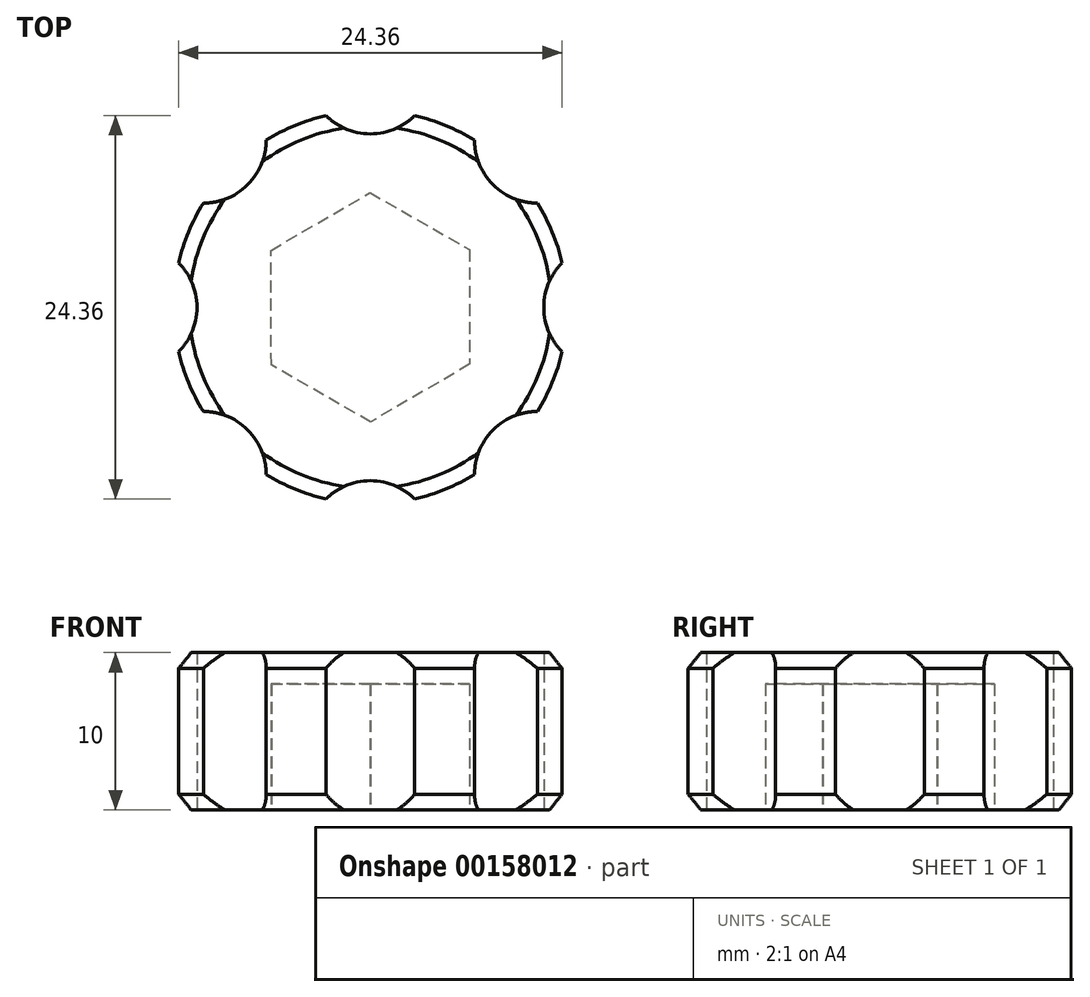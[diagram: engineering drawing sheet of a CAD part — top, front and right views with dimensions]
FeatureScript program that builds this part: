
annotation { "Feature Type Name" : "Feature", "Feature Type Description" : "" }
export const myFeature = defineFeature(function(context is Context, id is Id, definition is map)
    precondition{}
    {
        {
            var Q0;
            Q0=qCreatedBy(makeId("Top.planeOp"),FACE);
            var sketch = newSketch(context, id + "F0", { "sketchPlane" : qUnion([Q0])});
            skCircle(sketch, "E0", {"center": v(0, 0) * mm, "radius": 12.5 * mm});
            skCircle(sketch, "E1.cCircle", {"center": v(0, 0) * mm, "radius": 6.3 * mm, "construction": true});
            skLineSegment(sketch, "E1.0", {"start": v(6.31, -3.62) * mm, "end": v(0.02, -7.27) * mm});
            skLineSegment(sketch, "E1.1", {"start": v(0.02, -7.27) * mm, "end": v(-6.29, -3.66) * mm});
            skLineSegment(sketch, "E1.2", {"start": v(-6.29, -3.66) * mm, "end": v(-6.31, 3.62) * mm});
            skLineSegment(sketch, "E1.3", {"start": v(-6.31, 3.62) * mm, "end": v(-0.02, 7.27) * mm});
            skLineSegment(sketch, "E1.4", {"start": v(-0.02, 7.27) * mm, "end": v(6.29, 3.66) * mm});
            skLineSegment(sketch, "E1.5", {"start": v(6.29, 3.66) * mm, "end": v(6.31, -3.62) * mm});
            skPoint(sketch, "E1.0.midPoint", {"position": v(3.17, -5.45) * mm});
            skCircle(sketch, "E2", {"center": v(0, 15.01) * mm, "radius": 4 * mm});
            skCircle(sketch, "E3.1.0", {"center": v(-10.62, 10.62) * mm, "radius": 4 * mm});
            skCircle(sketch, "E3.2.0", {"center": v(-15.01, 0) * mm, "radius": 4 * mm});
            skCircle(sketch, "E4.1.3.0", {"center": v(-10.62, -10.62) * mm, "radius": 4 * mm});
            skCircle(sketch, "E4.1.4.0", {"center": v(0, -15.01) * mm, "radius": 4 * mm});
            skCircle(sketch, "E4.1.5.0", {"center": v(10.62, -10.62) * mm, "radius": 4 * mm});
            skCircle(sketch, "E5.1.6.0", {"center": v(15.01, 0) * mm, "radius": 4 * mm});
            skCircle(sketch, "E5.1.7.0", {"center": v(10.62, 10.62) * mm, "radius": 4 * mm});
            skSolve(sketch);
        }
        {
            var Q0;
            Q0=makeQuery(id+"F0.imprint","IMPRINT",FACE,{"disambiguationData":[TD([[makeQuery(id+"F0.imprint","IMPRINT",EDGE,{"derivedFrom":sQuery(id+"F0.wireOp",EDGE,"E1.0")}),1.0]])]});
            var Q1;
            Q1=makeQuery(id+"F0.imprint","IMPRINT",FACE,{"disambiguationData":[TD([[makeQuery(id+"F0.imprint","IMPRINT",EDGE,{"derivedFrom":sQuery(id+"F0.wireOp",EDGE,"E1.0")}),-1.0]])]});
            extrude(context, id + "F1", {"entities" : qUnion([Q0, Q1]), "depth" : 10 * mm});
        }
        {
            var Q0;
            Q0=makeQuery(id+"F0.imprint","IMPRINT",FACE,{"disambiguationData":[TD([[makeQuery(id+"F0.imprint","IMPRINT",EDGE,{"derivedFrom":sQuery(id+"F0.wireOp",EDGE,"E1.0")}),-1.0]])]});
            extrude(context, id + "F2", {"entities" : qUnion([Q0]), "operationType" : NewBodyOperationType.REMOVE, "depth" : 8 * mm});
        }
        {
            var Q0;
            {var subQ0=sQuery(id+"F0.wireOp",EDGE,"E0");Q0=makeQuery(id+"F1.opExtrude","CAP_EDGE",EDGE,{"disambiguationData":[OSD([subQ0]),TDD([makeQuery(id+"F0.imprint","IMPRINT",EDGE,{"disambiguationData":[TD([[makeQuery(id+"F0.imprint","INTERSECT",VERTEX,{"disambiguationData":[OD(1.0)],"derivedFrom":[subQ0,sQuery(id+"F0.wireOp",EDGE,"E4.1.5.0")]}),-1.0]])],"derivedFrom":subQ0})])],"isStart":false});}
            var Q1;
            {var subQ0=sQuery(id+"F0.wireOp",EDGE,"E0");Q1=makeQuery(id+"F1.opExtrude","CAP_EDGE",EDGE,{"disambiguationData":[OSD([subQ0]),TDD([makeQuery(id+"F0.imprint","IMPRINT",EDGE,{"disambiguationData":[TD([[makeQuery(id+"F0.imprint","INTERSECT",VERTEX,{"disambiguationData":[OD(0.0)],"derivedFrom":[subQ0,sQuery(id+"F0.wireOp",EDGE,"E5.1.7.0")]}),1.0]])],"derivedFrom":subQ0})])],"isStart":false});}
            var Q2;
            {var subQ0=sQuery(id+"F0.wireOp",EDGE,"E0");Q2=makeQuery(id+"F1.opExtrude","CAP_EDGE",EDGE,{"disambiguationData":[OSD([subQ0]),TDD([makeQuery(id+"F0.imprint","IMPRINT",EDGE,{"disambiguationData":[TD([[makeQuery(id+"F0.imprint","INTERSECT",VERTEX,{"disambiguationData":[OD(1.0)],"derivedFrom":[subQ0,sQuery(id+"F0.wireOp",EDGE,"E5.1.7.0")]}),-1.0]])],"derivedFrom":subQ0})])],"isStart":false});}
            var Q3;
            {var subQ0=sQuery(id+"F0.wireOp",EDGE,"E0");Q3=makeQuery(id+"F1.opExtrude","CAP_EDGE",EDGE,{"disambiguationData":[OSD([subQ0]),TDD([makeQuery(id+"F0.imprint","IMPRINT",EDGE,{"disambiguationData":[TD([[makeQuery(id+"F0.imprint","INTERSECT",VERTEX,{"disambiguationData":[OD(1.0)],"derivedFrom":[subQ0,sQuery(id+"F0.wireOp",EDGE,"E2")]}),-1.0]])],"derivedFrom":subQ0})])],"isStart":false});}
            var Q4;
            {var subQ0=sQuery(id+"F0.wireOp",EDGE,"E0");Q4=makeQuery(id+"F1.opExtrude","CAP_EDGE",EDGE,{"disambiguationData":[OSD([subQ0]),TDD([makeQuery(id+"F0.imprint","IMPRINT",EDGE,{"disambiguationData":[TD([[makeQuery(id+"F0.imprint","INTERSECT",VERTEX,{"disambiguationData":[OD(1.0)],"derivedFrom":[subQ0,sQuery(id+"F0.wireOp",EDGE,"E3.1.0")]}),-1.0]])],"derivedFrom":subQ0})])],"isStart":false});}
            var Q5;
            {var subQ0=sQuery(id+"F0.wireOp",EDGE,"E0");Q5=makeQuery(id+"F1.opExtrude","CAP_EDGE",EDGE,{"disambiguationData":[OSD([subQ0]),TDD([makeQuery(id+"F0.imprint","IMPRINT",EDGE,{"disambiguationData":[TD([[makeQuery(id+"F0.imprint","INTERSECT",VERTEX,{"disambiguationData":[OD(1.0)],"derivedFrom":[subQ0,sQuery(id+"F0.wireOp",EDGE,"E3.2.0")]}),-1.0]])],"derivedFrom":subQ0})])],"isStart":false});}
            var Q6;
            {var subQ0=sQuery(id+"F0.wireOp",EDGE,"E0");Q6=makeQuery(id+"F1.opExtrude","CAP_EDGE",EDGE,{"disambiguationData":[OSD([subQ0]),TDD([makeQuery(id+"F0.imprint","IMPRINT",EDGE,{"disambiguationData":[TD([[makeQuery(id+"F0.imprint","INTERSECT",VERTEX,{"disambiguationData":[OD(1.0)],"derivedFrom":[subQ0,sQuery(id+"F0.wireOp",EDGE,"E4.1.3.0")]}),-1.0]])],"derivedFrom":subQ0})])],"isStart":false});}
            var Q7;
            {var subQ0=sQuery(id+"F0.wireOp",EDGE,"E0");Q7=makeQuery(id+"F1.opExtrude","CAP_EDGE",EDGE,{"disambiguationData":[OSD([subQ0]),TDD([makeQuery(id+"F0.imprint","IMPRINT",EDGE,{"disambiguationData":[TD([[makeQuery(id+"F0.imprint","INTERSECT",VERTEX,{"disambiguationData":[OD(1.0)],"derivedFrom":[subQ0,sQuery(id+"F0.wireOp",EDGE,"E4.1.4.0")]}),-1.0]])],"derivedFrom":subQ0})])],"isStart":false});}
            var Q8;
            {var subQ0=sQuery(id+"F0.wireOp",EDGE,"E0");Q8=makeQuery(id+"F1.opExtrude","CAP_EDGE",EDGE,{"disambiguationData":[OSD([subQ0]),TDD([makeQuery(id+"F0.imprint","IMPRINT",EDGE,{"disambiguationData":[TD([[makeQuery(id+"F0.imprint","INTERSECT",VERTEX,{"disambiguationData":[OD(1.0)],"derivedFrom":[subQ0,sQuery(id+"F0.wireOp",EDGE,"E4.1.4.0")]}),-1.0]])],"derivedFrom":subQ0})])],"isStart":true});}
            var Q9;
            {var subQ0=sQuery(id+"F0.wireOp",EDGE,"E0");Q9=makeQuery(id+"F1.opExtrude","CAP_EDGE",EDGE,{"disambiguationData":[OSD([subQ0]),TDD([makeQuery(id+"F0.imprint","IMPRINT",EDGE,{"disambiguationData":[TD([[makeQuery(id+"F0.imprint","INTERSECT",VERTEX,{"disambiguationData":[OD(1.0)],"derivedFrom":[subQ0,sQuery(id+"F0.wireOp",EDGE,"E4.1.5.0")]}),-1.0]])],"derivedFrom":subQ0})])],"isStart":true});}
            var Q10;
            {var subQ0=sQuery(id+"F0.wireOp",EDGE,"E0");Q10=makeQuery(id+"F1.opExtrude","CAP_EDGE",EDGE,{"disambiguationData":[OSD([subQ0]),TDD([makeQuery(id+"F0.imprint","IMPRINT",EDGE,{"disambiguationData":[TD([[makeQuery(id+"F0.imprint","INTERSECT",VERTEX,{"disambiguationData":[OD(0.0)],"derivedFrom":[subQ0,sQuery(id+"F0.wireOp",EDGE,"E5.1.7.0")]}),1.0]])],"derivedFrom":subQ0})])],"isStart":true});}
            var Q11;
            {var subQ0=sQuery(id+"F0.wireOp",EDGE,"E0");Q11=makeQuery(id+"F1.opExtrude","CAP_EDGE",EDGE,{"disambiguationData":[OSD([subQ0]),TDD([makeQuery(id+"F0.imprint","IMPRINT",EDGE,{"disambiguationData":[TD([[makeQuery(id+"F0.imprint","INTERSECT",VERTEX,{"disambiguationData":[OD(1.0)],"derivedFrom":[subQ0,sQuery(id+"F0.wireOp",EDGE,"E5.1.7.0")]}),-1.0]])],"derivedFrom":subQ0})])],"isStart":true});}
            var Q12;
            {var subQ0=sQuery(id+"F0.wireOp",EDGE,"E0");Q12=makeQuery(id+"F1.opExtrude","CAP_EDGE",EDGE,{"disambiguationData":[OSD([subQ0]),TDD([makeQuery(id+"F0.imprint","IMPRINT",EDGE,{"disambiguationData":[TD([[makeQuery(id+"F0.imprint","INTERSECT",VERTEX,{"disambiguationData":[OD(1.0)],"derivedFrom":[subQ0,sQuery(id+"F0.wireOp",EDGE,"E2")]}),-1.0]])],"derivedFrom":subQ0})])],"isStart":true});}
            var Q13;
            {var subQ0=sQuery(id+"F0.wireOp",EDGE,"E0");Q13=makeQuery(id+"F1.opExtrude","CAP_EDGE",EDGE,{"disambiguationData":[OSD([subQ0]),TDD([makeQuery(id+"F0.imprint","IMPRINT",EDGE,{"disambiguationData":[TD([[makeQuery(id+"F0.imprint","INTERSECT",VERTEX,{"disambiguationData":[OD(1.0)],"derivedFrom":[subQ0,sQuery(id+"F0.wireOp",EDGE,"E3.1.0")]}),-1.0]])],"derivedFrom":subQ0})])],"isStart":true});}
            var Q14;
            {var subQ0=sQuery(id+"F0.wireOp",EDGE,"E0");Q14=makeQuery(id+"F1.opExtrude","CAP_EDGE",EDGE,{"disambiguationData":[OSD([subQ0]),TDD([makeQuery(id+"F0.imprint","IMPRINT",EDGE,{"disambiguationData":[TD([[makeQuery(id+"F0.imprint","INTERSECT",VERTEX,{"disambiguationData":[OD(1.0)],"derivedFrom":[subQ0,sQuery(id+"F0.wireOp",EDGE,"E3.2.0")]}),-1.0]])],"derivedFrom":subQ0})])],"isStart":true});}
            var Q15;
            {var subQ0=sQuery(id+"F0.wireOp",EDGE,"E0");Q15=makeQuery(id+"F1.opExtrude","CAP_EDGE",EDGE,{"disambiguationData":[OSD([subQ0]),TDD([makeQuery(id+"F0.imprint","IMPRINT",EDGE,{"disambiguationData":[TD([[makeQuery(id+"F0.imprint","INTERSECT",VERTEX,{"disambiguationData":[OD(1.0)],"derivedFrom":[subQ0,sQuery(id+"F0.wireOp",EDGE,"E4.1.3.0")]}),-1.0]])],"derivedFrom":subQ0})])],"isStart":true});}
            chamfer(context, id + "F3", {"entities" : qUnion([Q0, Q1, Q2, Q3, Q4, Q5, Q6, Q7, Q8, Q9, Q10, Q11, Q12, Q13, Q14, Q15]), "width" : 1 * mm, "tangentPropagation" : true});
        }
    });
